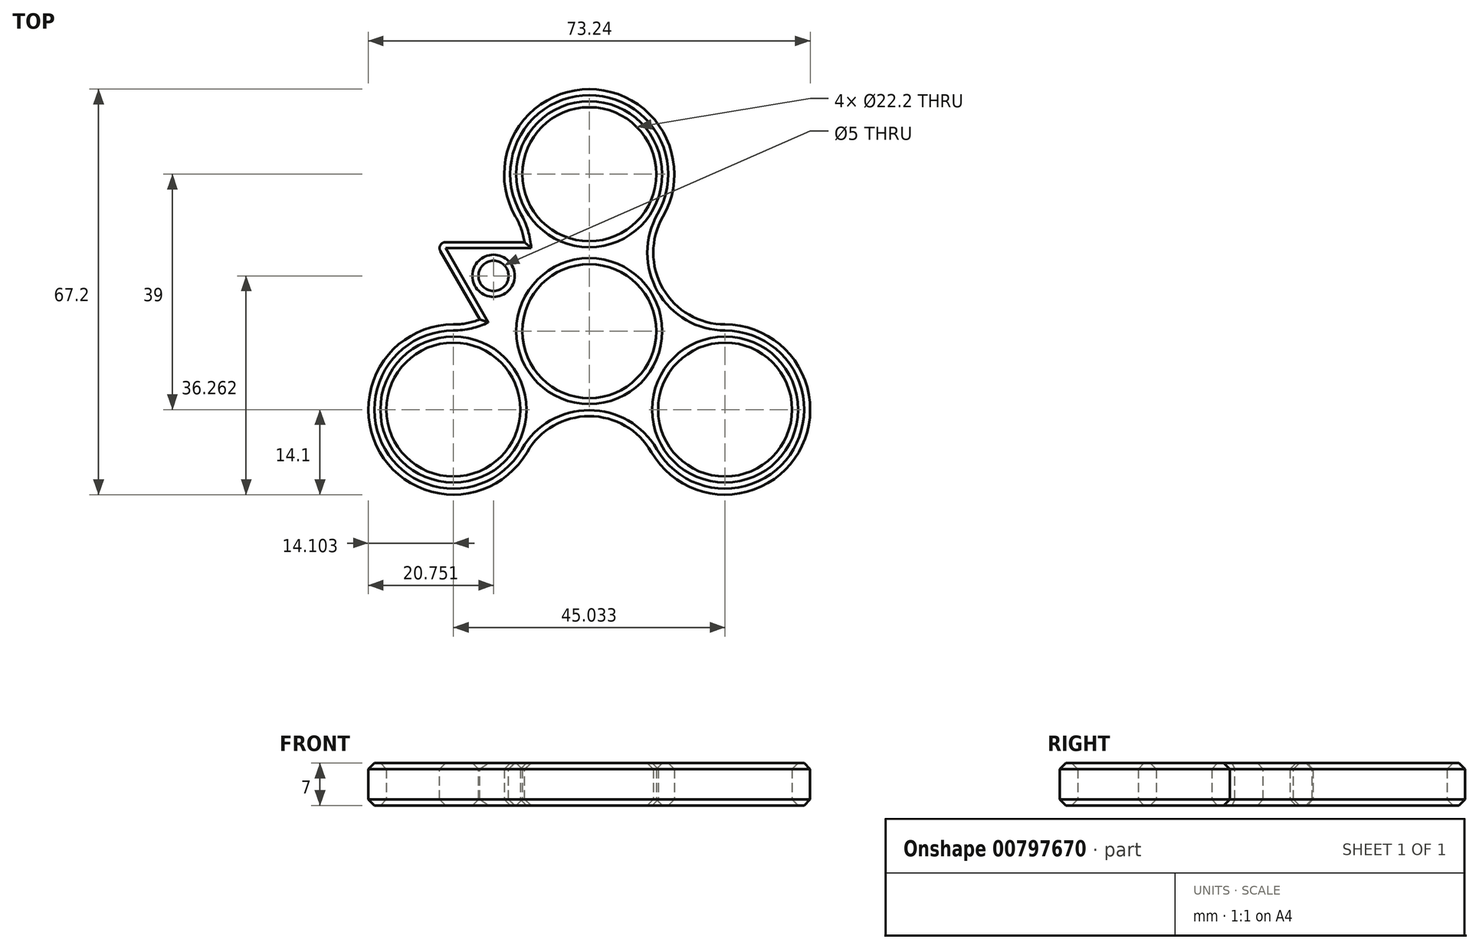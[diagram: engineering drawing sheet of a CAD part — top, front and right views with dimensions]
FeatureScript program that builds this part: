
annotation { "Feature Type Name" : "Feature", "Feature Type Description" : "" }
export const myFeature = defineFeature(function(context is Context, id is Id, definition is map)
    precondition{}
    {
        {
            var Q0;
            Q0=qCreatedBy(makeId("Top.planeOp"),FACE);
            var sketch = newSketch(context, id + "F0", { "sketchPlane" : qUnion([Q0])});
            skCircle(sketch, "E0", {"center": v(0, 0) * mm, "radius": 11.1 * mm});
            skCircle(sketch, "E1.cCircle", {"center": v(0, 0) * mm, "radius": 13 * mm, "construction": true});
            skLineSegment(sketch, "E1.0", {"start": v(22.52, -13) * mm, "end": v(-22.52, -13) * mm, "construction": true});
            skLineSegment(sketch, "E1.1", {"start": v(-22.52, -13) * mm, "end": v(0, 26) * mm, "construction": true});
            skLineSegment(sketch, "E1.2", {"start": v(0, 26) * mm, "end": v(22.52, -13) * mm, "construction": true});
            skPoint(sketch, "E1.0.midPoint", {"position": v(0, -13) * mm});
            skCircle(sketch, "E2", {"center": v(0, 26) * mm, "radius": 11.1 * mm});
            skLineSegment(sketch, "E3", {"start": v(0, 0) * mm, "end": v(-11.26, 6.5) * mm});
            skLineSegment(sketch, "E4", {"start": v(-11.26, 6.5) * mm, "end": v(11.26, 6.5) * mm, "construction": true});
            skLineSegment(sketch, "E5", {"start": v(11.26, 6.5) * mm, "end": v(0, 0) * mm});
            skLineSegment(sketch, "E6", {"start": v(0, -13) * mm, "end": v(0, 0) * mm, "construction": true});
            skLineSegment(sketch, "E7", {"start": v(11.26, 6.5) * mm, "end": v(0, -13) * mm, "construction": true});
            skLineSegment(sketch, "E8", {"start": v(-11.26, 6.5) * mm, "end": v(0, -13) * mm, "construction": true});
            skLineSegment(sketch, "E9", {"start": v(11.26, 6.5) * mm, "end": v(22.52, 13) * mm, "construction": true});
            skArc(sketch, "E10", {"start": v(12.21, 18.95) * mm, "mid": v(0, 40.1) * mm, "end": v(-12.21, 18.95) * mm});
            skArc(sketch, "E11", {"start": v(12.21, 7.05) * mm, "mid": v(10.62, 13) * mm, "end": v(12.21, 18.95) * mm});
            skArc(sketch, "E12.MirrorCS", {"start": v(-12.21, 7.05) * mm, "mid": v(-10.62, 13) * mm, "end": v(-12.21, 18.95) * mm});
            skCircle(sketch, "E13", {"center": v(0, 0) * mm, "radius": 14.1 * mm, "construction": true});
            skLineSegment(sketch, "E14", {"start": v(-12.21, 7.05) * mm, "end": v(-11.26, 6.5) * mm});
            skLineSegment(sketch, "E15", {"start": v(11.26, 6.5) * mm, "end": v(12.21, 7.05) * mm});
            skSolve(sketch);
        }
        {
            var Q0;
            Q0=makeQuery(id+"F0.imprint","IMPRINT",FACE,{"disambiguationData":[TD([[makeQuery(id+"F0.imprint","IMPRINT",EDGE,{"derivedFrom":sQuery(id+"F0.wireOp",EDGE,"E2")}),-1.0]])]});
            extrude(context, id + "F1", {"entities" : qUnion([Q0]), "depth" : 7 * mm, "offsetDistance" : 25 * mm});
        }
        {
            var Q0;
            Q0=makeQuery(id+"F1.opExtrude","SWEPT_BODY",BODY,{"disambiguationData":[OSD([sQuery(id+"F0.wireOp",EDGE,"E0"),sQuery(id+"F0.wireOp",EDGE,"E2"),sQuery(id+"F0.wireOp",EDGE,"E3"),sQuery(id+"F0.wireOp",EDGE,"E5"),sQuery(id+"F0.wireOp",EDGE,"E10"),sQuery(id+"F0.wireOp",EDGE,"FyzykIo4-7ABL-2cN2-SJu5-aql6egmz9Ra5"),sQuery(id+"F0.wireOp",EDGE,"948eeb6a-f036-419e-b3b6-321a4cbb431c0.MirrorCS")])]});
            var Q1;
            Q1=sQuery(id+"F0.wireOp",EDGE,"E0");
            circularPattern(context, id + "F2", {"operationType" : NewBodyOperationType.ADD, "entities" : qUnion([Q0]), "axis" : qUnion([Q1]), "angle" : 360 * degree, "instanceCount" : 3, "equalSpace" : true});
        }
        {
            var Q0;
            {var subQ0=makeQuery(id+"F1.opExtrude","CAP_FACE",FACE,{"disambiguationData":[OSD([sQuery(id+"F0.wireOp",EDGE,"E0"),sQuery(id+"F0.wireOp",EDGE,"E2"),sQuery(id+"F0.wireOp",EDGE,"E3"),sQuery(id+"F0.wireOp",EDGE,"E5"),sQuery(id+"F0.wireOp",EDGE,"E10"),sQuery(id+"F0.wireOp",EDGE,"FyzykIo4-7ABL-2cN2-SJu5-aql6egmz9Ra5"),sQuery(id+"F0.wireOp",EDGE,"948eeb6a-f036-419e-b3b6-321a4cbb431c0.MirrorCS")])],"isStart":false});Q0=makeQuery(id+"F2.boolean.opBoolean","MERGE",FACE,{"derivedFrom":[subQ0,makeQuery(id+"F2.opPattern","COPY",FACE,{"derivedFrom":subQ0,"instanceName":"1"}),makeQuery(id+"F2.opPattern","COPY",FACE,{"derivedFrom":subQ0,"instanceName":"2"})]});}
            var sketch = newSketch(context, id + "F3", { "sketchPlane" : qUnion([Q0])});
            skPoint(sketch, "E16", {"position": v(-6.4, 18.9) * mm});
            skSolve(sketch);
        }
        {
            var Q0;
            {var subQ1=makeQuery(id+"F1.opExtrude","CAP_EDGE",EDGE,{"disambiguationData":[OSD([sQuery(id+"F0.wireOp",EDGE,"E2")])],"isStart":false});Q0=makeQuery(id+"F3.imprint","IMPRINT",FACE,{"disambiguationData":[TD([[makeQuery(id+"F3.imprint","IMPRINT",EDGE,{"derivedFrom":subQ1}),-1.0]])]});}
            var sketch = newSketch(context, id + "F4", { "sketchPlane" : qUnion([Q0])});
            skCircle(sketch, "E17.cCircle", {"center": v(-15.87, 9.16) * mm, "radius": 5.58 * mm, "construction": true});
            skLineSegment(sketch, "E17.0", {"start": v(-6.2, 14.74) * mm, "end": v(-15.87, -2) * mm});
            skLineSegment(sketch, "E17.1", {"start": v(-15.87, -2) * mm, "end": v(-25.54, 14.74) * mm});
            skLineSegment(sketch, "E17.2", {"start": v(-25.54, 14.74) * mm, "end": v(-6.2, 14.74) * mm});
            skPoint(sketch, "E17.0.midPoint", {"position": v(-11.03, 6.37) * mm});
            skLineSegment(sketch, "E18", {"start": v(0, 0) * mm, "end": v(0, 58.47) * mm, "construction": true});
            skLineSegment(sketch, "E19", {"start": v(0, 0) * mm, "end": v(-15.87, 9.16) * mm, "construction": true});
            skSolve(sketch);
        }
        {
            var Q0;
            {var subQ0=sQuery(id+"F4.wireOp",EDGE,"E17.2");var subQ1=sQuery(id+"F4.wireOp",EDGE,"E17.1");var subQ2=makeQuery(id+"F4.imprint","INTERSECT",VERTEX,{"derivedFrom":[subQ1,subQ0]});Q0=makeQuery(id+"F4.imprint","IMPRINT",FACE,{"disambiguationData":[TD([[makeQuery(id+"F4.imprint","IMPRINT",EDGE,{"disambiguationData":[TD([[subQ2,1.0]])],"derivedFrom":subQ1}),-1.0]])]});}
            extrude(context, id + "F5", {"entities" : qUnion([Q0]), "operationType" : NewBodyOperationType.ADD, "oppositeDirection" : true, "depth" : 7 * mm, "offsetDistance" : 25 * mm});
        }
        {
            var Q0;
            Q0=sQuery(id+"F4.wireOp",VERTEX,"E19.end");
            var Q1;
            Q1=makeQuery(id+"F1.opExtrude","SWEPT_BODY",BODY,{"disambiguationData":[OSD([sQuery(id+"F0.wireOp",EDGE,"E0"),sQuery(id+"F0.wireOp",EDGE,"E2"),sQuery(id+"F0.wireOp",EDGE,"E3"),sQuery(id+"F0.wireOp",EDGE,"E5"),sQuery(id+"F0.wireOp",EDGE,"E10"),sQuery(id+"F0.wireOp",EDGE,"E11"),sQuery(id+"F0.wireOp",EDGE,"E12.MirrorCS"),sQuery(id+"F0.wireOp",EDGE,"E14"),sQuery(id+"F0.wireOp",EDGE,"E15")])]});
            hole(context, id + "F6", {"style" : HoleStyle.SIMPLE, "endStyle" : HoleEndStyle.THROUGH, "holeDiameter" : 5 * mm, "majorDiameter" : 5 * mm, "isTappedThrough" : true, "tappedDepth" : 12 * mm, "tapClearance" : 3, "locations" : qUnion([Q0]), "scope" : qUnion([Q1])});
        }
        {
            var Q0;
            Q0=makeQuery(id+"FiSt6mcPyRZ0xXD_1.2.F5.opExtrude","SWEPT_EDGE",EDGE,{"disambiguationData":[OSD([sQuery(id+"F4.wireOp",EDGE,"E17.1"),sQuery(id+"F4.wireOp",EDGE,"E17.2")])]});
            var Q1;
            Q1=makeQuery(id+"FiSt6mcPyRZ0xXD_1.1.F5.opExtrude","SWEPT_EDGE",EDGE,{"disambiguationData":[OSD([sQuery(id+"F4.wireOp",EDGE,"E17.1"),sQuery(id+"F4.wireOp",EDGE,"E17.2")])]});
            var Q2;
            Q2=makeQuery(id+"F5.opExtrude","SWEPT_EDGE",EDGE,{"disambiguationData":[OSD([sQuery(id+"F4.wireOp",EDGE,"E17.1"),sQuery(id+"F4.wireOp",EDGE,"E17.2")])]});
            fillet(context, id + "F7", {"entities" : qUnion([Q0, Q1, Q2]), "radius" : 1 * mm, "tangentPropagation" : true, "allowEdgeOverflow" : false});
        }
        {
            var Q0;
            {var subQ0=sQuery(id+"F4.wireOp",EDGE,"E17.2");var subQ1=sQuery(id+"F4.wireOp",EDGE,"E17.1");var subQ2=sQuery(id+"F0.wireOp",EDGE,"E12.MirrorCS");var subQ3=sQuery(id+"F0.wireOp",EDGE,"E11");var subQ4=makeQuery(id+"F1.opExtrude","CAP_FACE",FACE,{"disambiguationData":[OSD([sQuery(id+"F0.wireOp",EDGE,"E0"),sQuery(id+"F0.wireOp",EDGE,"E2"),sQuery(id+"F0.wireOp",EDGE,"E3"),sQuery(id+"F0.wireOp",EDGE,"E5"),sQuery(id+"F0.wireOp",EDGE,"E10"),subQ3,subQ2,sQuery(id+"F0.wireOp",EDGE,"E14"),sQuery(id+"F0.wireOp",EDGE,"E15")])],"isStart":false});Q0=makeQuery(id+"FiSt6mcPyRZ0xXD_1.2.F5.boolean.opBoolean","MERGE",FACE,{"derivedFrom":[makeQuery(id+"FiSt6mcPyRZ0xXD_1.1.F5.boolean.opBoolean","MERGE",FACE,{"derivedFrom":[makeQuery(id+"F5.boolean.opBoolean","MERGE",FACE,{"derivedFrom":[makeQuery(id+"F2.boolean.opBoolean","MERGE",FACE,{"derivedFrom":[subQ4,makeQuery(id+"F2.opPattern","COPY",FACE,{"derivedFrom":subQ4,"instanceName":"1"}),makeQuery(id+"F2.opPattern","COPY",FACE,{"derivedFrom":subQ4,"instanceName":"2"})]}),makeQuery(id+"F5.opExtrude","CAP_FACE",FACE,{"disambiguationData":[OSD([subQ3,subQ2,subQ1,subQ0])],"isStart":true})]}),makeQuery(id+"FiSt6mcPyRZ0xXD_1.1.F5.opExtrude","CAP_FACE",FACE,{"disambiguationData":[OSD([subQ3,subQ2,subQ1,subQ0])],"isStart":true})]}),makeQuery(id+"FiSt6mcPyRZ0xXD_1.2.F5.opExtrude","CAP_FACE",FACE,{"disambiguationData":[OSD([subQ3,subQ2,subQ1,subQ0])],"isStart":true})]});}
            var Q1;
            {var subQ0=sQuery(id+"F4.wireOp",EDGE,"E17.2");var subQ1=sQuery(id+"F4.wireOp",EDGE,"E17.1");var subQ2=sQuery(id+"F0.wireOp",EDGE,"E12.MirrorCS");var subQ3=sQuery(id+"F0.wireOp",EDGE,"E11");var subQ4=makeQuery(id+"F1.opExtrude","CAP_FACE",FACE,{"disambiguationData":[OSD([sQuery(id+"F0.wireOp",EDGE,"E0"),sQuery(id+"F0.wireOp",EDGE,"E2"),sQuery(id+"F0.wireOp",EDGE,"E3"),sQuery(id+"F0.wireOp",EDGE,"E5"),sQuery(id+"F0.wireOp",EDGE,"E10"),subQ3,subQ2,sQuery(id+"F0.wireOp",EDGE,"E14"),sQuery(id+"F0.wireOp",EDGE,"E15")])],"isStart":true});Q1=makeQuery(id+"FiSt6mcPyRZ0xXD_1.2.F5.boolean.opBoolean","MERGE",FACE,{"derivedFrom":[makeQuery(id+"FiSt6mcPyRZ0xXD_1.1.F5.boolean.opBoolean","MERGE",FACE,{"derivedFrom":[makeQuery(id+"F5.boolean.opBoolean","MERGE",FACE,{"derivedFrom":[makeQuery(id+"F2.boolean.opBoolean","MERGE",FACE,{"derivedFrom":[subQ4,makeQuery(id+"F2.opPattern","COPY",FACE,{"derivedFrom":subQ4,"instanceName":"1"}),makeQuery(id+"F2.opPattern","COPY",FACE,{"derivedFrom":subQ4,"instanceName":"2"})]}),makeQuery(id+"F5.opExtrude","CAP_FACE",FACE,{"disambiguationData":[OSD([subQ3,subQ2,subQ1,subQ0])],"isStart":false})]}),makeQuery(id+"FiSt6mcPyRZ0xXD_1.1.F5.opExtrude","CAP_FACE",FACE,{"disambiguationData":[OSD([subQ3,subQ2,subQ1,subQ0])],"isStart":false})]}),makeQuery(id+"FiSt6mcPyRZ0xXD_1.2.F5.opExtrude","CAP_FACE",FACE,{"disambiguationData":[OSD([subQ3,subQ2,subQ1,subQ0])],"isStart":false})]});}
            chamfer(context, id + "F8", {"entities" : qUnion([Q0, Q1]), "width" : 1 * mm, "tangentPropagation" : true});
        }
    });
